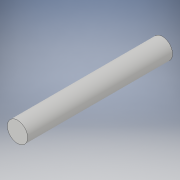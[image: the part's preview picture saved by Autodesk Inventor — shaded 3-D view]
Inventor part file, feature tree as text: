
AUTODESK INVENTOR PART (.ipt)
format: ipt  version: 2019 (Build 230136000, 136)  size: 207,360 bytes
history: native  units: mm
features: extrude x1, sketch x1
ambient origin geometry x8: Origin, YZ Plane, XZ Plane, XY Plane, X Axis, Y Axis, Z Axis, Center Point
bodies: Solid1 (feature_tree)
feature tree (2):
  extrude  "Extrusion1"  Depth=50.0mm TaperAngle=0.0deg
  sketch  "Sketch1"  dims[d0=7.0mm d1=50.0mm d2=0.0mm]
